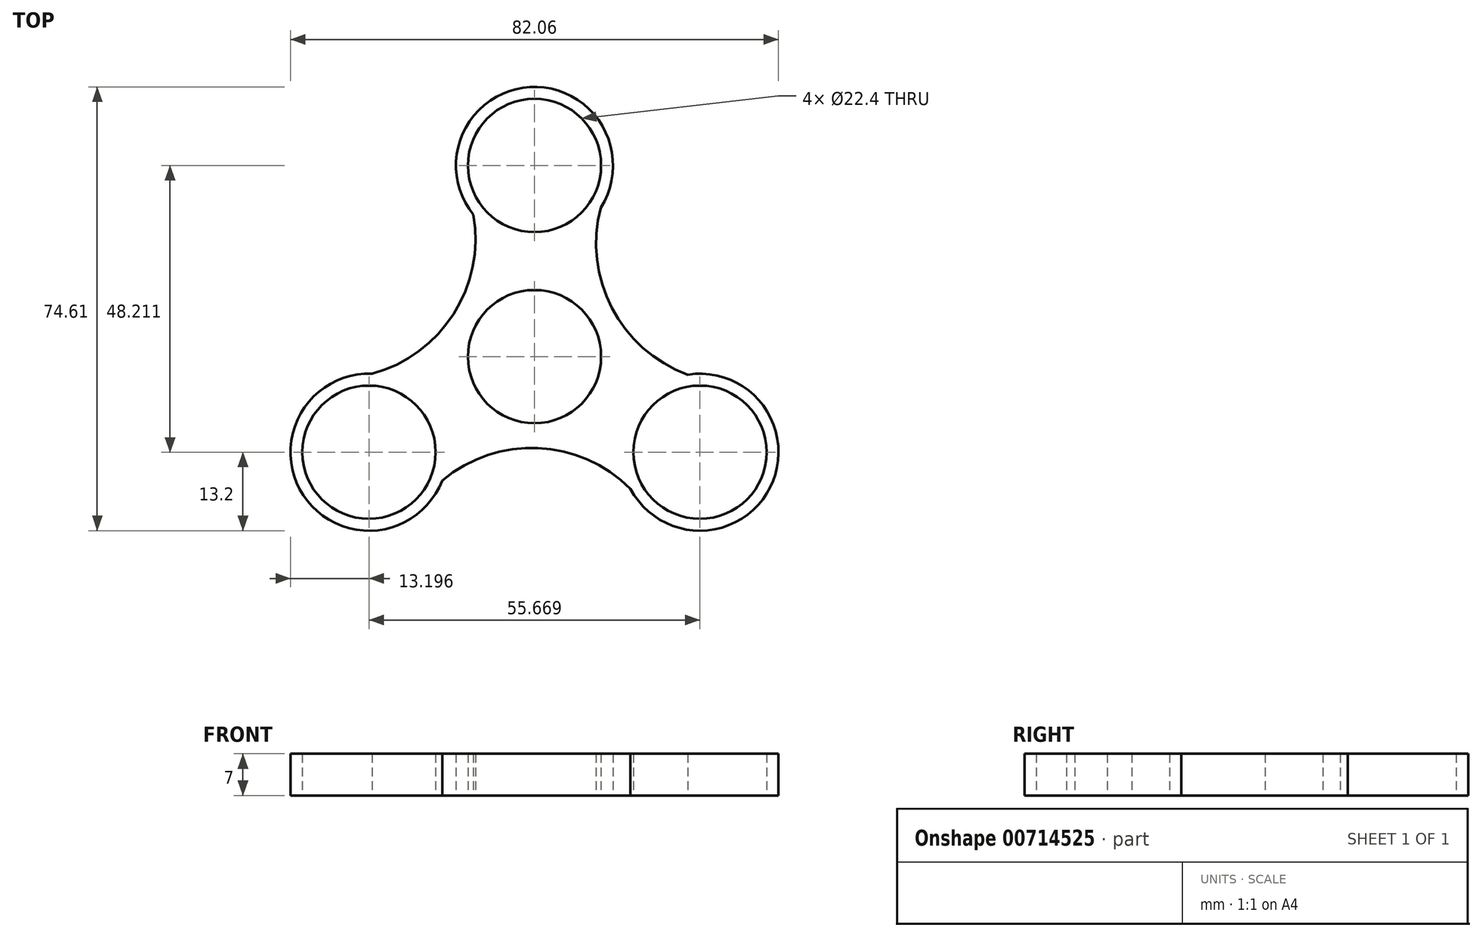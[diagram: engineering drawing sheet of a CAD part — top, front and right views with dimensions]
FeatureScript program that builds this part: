
annotation { "Feature Type Name" : "Feature", "Feature Type Description" : "" }
export const myFeature = defineFeature(function(context is Context, id is Id, definition is map)
    precondition{}
    {
        {
            var Q0;
            Q0=qCreatedBy(makeId("Top.planeOp"),FACE);
            var sketch = newSketch(context, id + "F0", { "sketchPlane" : qUnion([Q0])});
            skCircle(sketch, "E0", {"center": v(0, 0) * mm, "radius": 11.2 * mm});
            skCircle(sketch, "E1", {"center": v(0, 32.14) * mm, "radius": 11.2 * mm});
            skArc(sketch, "E2", {"start": v(11.16, 25.1) * mm, "mid": v(-0.76, 45.32) * mm, "end": v(-10.27, 23.85) * mm});
            skArc(sketch, "E3.1.0", {"start": v(-27.31, -2.88) * mm, "mid": v(-38.86, -23.32) * mm, "end": v(-15.52, -20.82) * mm});
            skCircle(sketch, "E3.1.1", {"center": v(-27.83, -16.07) * mm, "radius": 11.2 * mm});
            skArc(sketch, "E3.2.0", {"start": v(16.15, -22.21) * mm, "mid": v(39.63, -22) * mm, "end": v(25.79, -3.03) * mm});
            skCircle(sketch, "E3.2.1", {"center": v(27.83, -16.07) * mm, "radius": 11.2 * mm});
            skArc(sketch, "E4", {"start": v(11.16, 25.1) * mm, "mid": v(13.02, 8.2) * mm, "end": v(25.79, -3.03) * mm});
            skArc(sketch, "E5.1.0", {"start": v(-27.31, -2.88) * mm, "mid": v(-13.6, 7.18) * mm, "end": v(-10.27, 23.85) * mm});
            skArc(sketch, "E5.2.0", {"start": v(16.15, -22.21) * mm, "mid": v(0.59, -15.38) * mm, "end": v(-15.52, -20.82) * mm});
            skSolve(sketch);
        }
        {
            var Q0;
            Q0=qSketchRegion(id+"F0",true);
            extrude(context, id + "F1", {"entities" : qUnion([Q0]), "depth" : 7 * mm, "offsetDistance" : 25 * mm});
        }
    });
